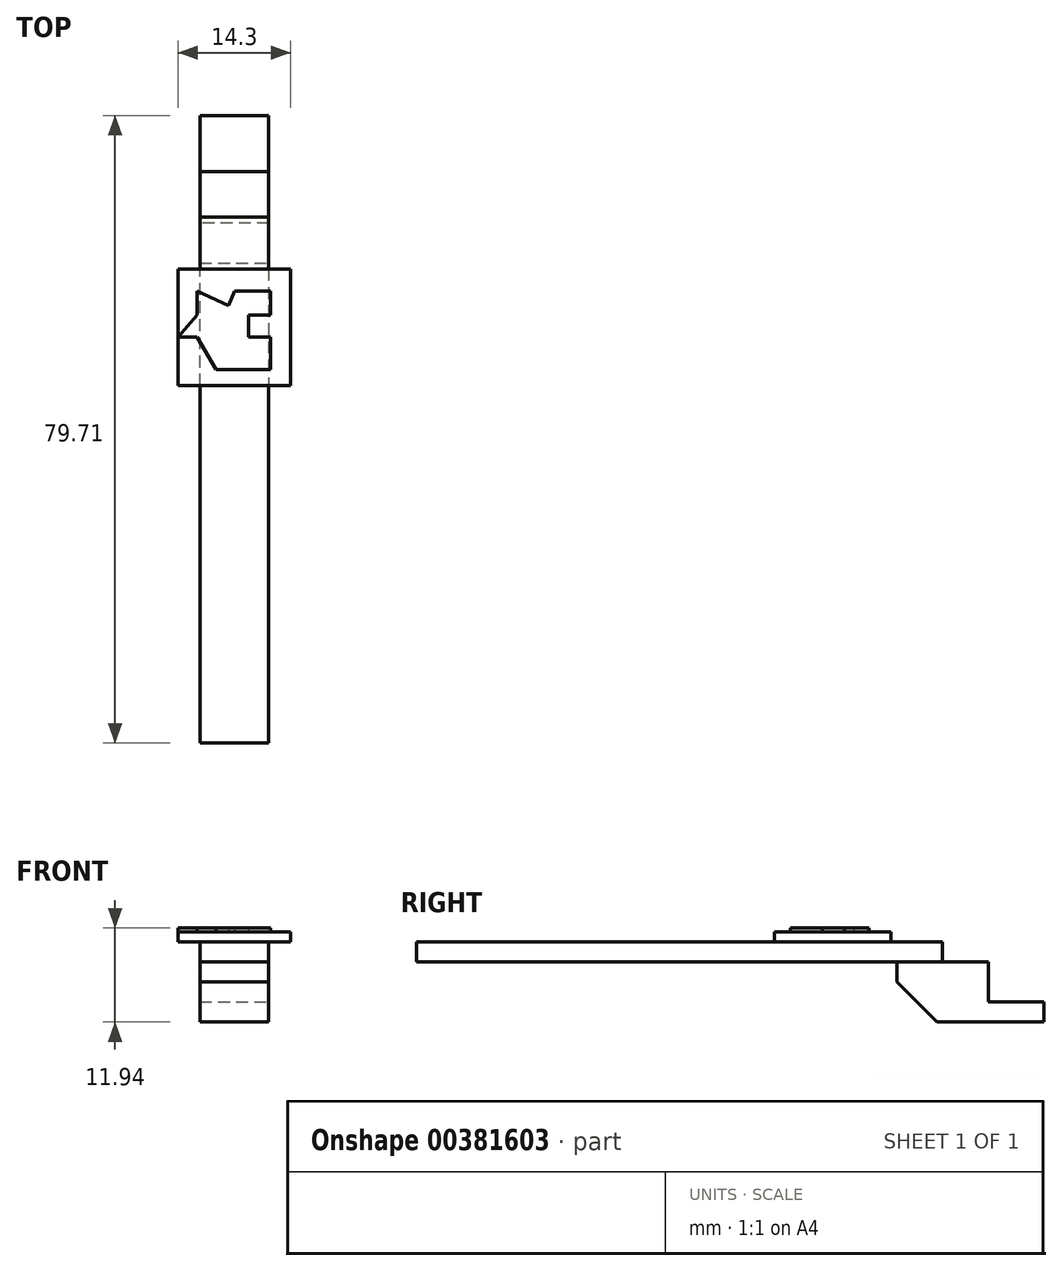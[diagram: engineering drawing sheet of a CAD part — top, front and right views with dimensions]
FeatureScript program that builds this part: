
annotation { "Feature Type Name" : "Feature", "Feature Type Description" : "" }
export const myFeature = defineFeature(function(context is Context, id is Id, definition is map)
    precondition{}
    {
        {
            var Q0;
            Q0=qCreatedBy(makeId("Top.planeOp"),FACE);
            var sketch = newSketch(context, id + "F0", { "sketchPlane" : qUnion([Q0])});
            skFitSpline(sketch, "E0", {"points": [v(0, 63.58) * mm, v(-18.17, 58.96) * mm, v(-23.3, 36.4) * mm, v(-12.53, 11.54) * mm, v(0, 6.16) * mm], "startDerivative": vector(-86.78, -3.86) * mm, "endDerivative": vector(63.99, -13.75) * mm});
            skFitSpline(sketch, "E1.MirrorCS", {"points": [v(0, 63.58) * mm, v(18.17, 58.96) * mm, v(23.3, 36.4) * mm, v(12.53, 11.54) * mm, v(0, 6.16) * mm], "startDerivative": vector(86.78, -3.86) * mm, "endDerivative": vector(-63.99, -13.75) * mm});
            skLineSegment(sketch, "E2", {"start": v(-4.37, 7.1) * mm, "end": v(-4.37, 0) * mm});
            skLineSegment(sketch, "E3", {"start": v(4.37, 7.1) * mm, "end": v(4.37, 0) * mm});
            skLineSegment(sketch, "E4", {"start": v(4.37, 0) * mm, "end": v(-4.37, 0) * mm});
            skLineSegment(sketch, "E5", {"start": v(-4.37, 7.1) * mm, "end": v(-4, 7.1) * mm});
            skLineSegment(sketch, "E6.trimOffspring", {"start": v(4, 7.1) * mm, "end": v(4.37, 7.1) * mm});
            skLineSegment(sketch, "E7", {"start": v(-4, 7.1) * mm, "end": v(4.37, 7.1) * mm});
            skLineSegment(sketch, "E8", {"start": v(-14.04, 53.47) * mm, "end": v(13.02, 53.47) * mm});
            skLineSegment(sketch, "E9", {"start": v(13.02, 21.06) * mm, "end": v(-14.04, 21.06) * mm});
            skLineSegment(sketch, "E10", {"start": v(-14.04, 49.9) * mm, "end": v(13.02, 49.9) * mm});
            skLineSegment(sketch, "E11", {"start": v(-14.04, 24.37) * mm, "end": v(13.02, 24.37) * mm});
            skLineSegment(sketch, "E12", {"start": v(-14.04, 34.58) * mm, "end": v(13.02, 34.58) * mm});
            skLineSegment(sketch, "E13", {"start": v(-14.04, 38.15) * mm, "end": v(13.02, 38.15) * mm});
            skLineSegment(sketch, "E14", {"start": v(13.02, 38.15) * mm, "end": v(13.02, 34.58) * mm});
            skLineSegment(sketch, "E15", {"start": v(13.02, 53.47) * mm, "end": v(13.02, 49.9) * mm});
            skLineSegment(sketch, "E16", {"start": v(-14.04, 53.47) * mm, "end": v(-14.04, 49.9) * mm});
            skLineSegment(sketch, "E17", {"start": v(-14.04, 38.15) * mm, "end": v(-14.04, 34.58) * mm});
            skLineSegment(sketch, "E18", {"start": v(-14.04, 24.37) * mm, "end": v(-14.04, 21.06) * mm});
            skLineSegment(sketch, "E19", {"start": v(13.02, 24.37) * mm, "end": v(13.02, 21.06) * mm});
            skLineSegment(sketch, "E20", {"start": v(-4.37, 0) * mm, "end": v(4.37, 0) * mm});
            skLineSegment(sketch, "E21", {"start": v(4.37, -11.61) * mm, "end": v(-4.37, -11.61) * mm});
            skLineSegment(sketch, "E22", {"start": v(-4.37, 0) * mm, "end": v(-4.37, -11.61) * mm});
            skLineSegment(sketch, "E23", {"start": v(4.37, -11.61) * mm, "end": v(4.37, 0) * mm});
            skSolve(sketch);
        }
        {
            var Q0;
            {var subQ0=sQuery(id+"F0.wireOp",EDGE,"E0");Q0=makeQuery(id+"F0.imprint","IMPRINT",FACE,{"disambiguationData":[TD([[makeQuery(id+"F0.imprint","IMPRINT",EDGE,{"derivedFrom":subQ0}),1.0]])]});}
            var Q1;
            Q1=makeQuery(id+"F0.imprint","IMPRINT",FACE,{"disambiguationData":[TD([[makeQuery(id+"F0.imprint","IMPRINT",EDGE,{"derivedFrom":sQuery(id+"F0.wireOp",EDGE,"E2")}),1.0]])]});
            extrude(context, id + "F1", {"entities" : qUnion([Q0, Q1]), "depth" : 2.54 * mm});
        }
        {
            var Q0;
            Q0=makeQuery(id+"F0.imprint","IMPRINT",FACE,{"disambiguationData":[TD([[makeQuery(id+"F0.imprint","IMPRINT",EDGE,{"derivedFrom":sQuery(id+"F0.wireOp",EDGE,"E21")}),-1.0]])]});
            extrude(context, id + "F2", {"entities" : qUnion([Q0]), "operationType" : NewBodyOperationType.ADD, "depth" : 7.62 * mm});
        }
        {
            var Q0;
            Q0=makeQuery(id+"F2.opExtrude","CAP_FACE",FACE,{"disambiguationData":[OSD([sQuery(id+"F0.wireOp",EDGE,"E21"),sQuery(id+"F0.wireOp",EDGE,"E22"),sQuery(id+"F0.wireOp",EDGE,"E20"),sQuery(id+"F0.wireOp",EDGE,"E23")])],"isStart":false});
            var sketch = newSketch(context, id + "F3", { "sketchPlane" : qUnion([Q0])});
            skLineSegment(sketch, "E24", {"start": v(-4.37, -5.8) * mm, "end": v(4.37, -5.8) * mm});
            skLineSegment(sketch, "E25", {"start": v(4.37, -5.8) * mm, "end": v(4.37, -72.6) * mm});
            skLineSegment(sketch, "E26", {"start": v(-4.37, -72.6) * mm, "end": v(-4.37, -5.8) * mm});
            skLineSegment(sketch, "E27", {"start": v(4.37, -70.31) * mm, "end": v(4.37, -72.6) * mm});
            skLineSegment(sketch, "E28", {"start": v(-4.37, -72.6) * mm, "end": v(4.37, -72.6) * mm});
            skSolve(sketch);
        }
        {
            var Q0;
            Q0 = qSketchRegion(id + "F3", true);
            extrude(context, id + "F4", {"entities" : qUnion([Q0]), "depth" : 2.54 * mm});
        }
        {
            var Q0;
            Q0=makeQuery(id+"F2.opExtrude","CAP_EDGE",EDGE,{"disambiguationData":[OSD([sQuery(id+"F0.wireOp",EDGE,"E21")])],"isStart":true});
            var Q1;
            Q1=makeQuery(id+"F2.opExtrude","CAP_EDGE",EDGE,{"disambiguationData":[OSD([sQuery(id+"F0.wireOp",EDGE,"E20")])],"isStart":false});
            chamfer(context, id + "F5", {"entities" : qUnion([Q0, Q1]), "width" : 5.08 * mm, "tangentPropagation" : true});
        }
        {
            var Q0;
            Q0=makeQuery(id+"F4.opExtrude","CAP_FACE",FACE,{"disambiguationData":[OSD([sQuery(id+"F3.wireOp",EDGE,"E24"),sQuery(id+"F3.wireOp",EDGE,"E25"),sQuery(id+"F3.wireOp",EDGE,"E26"),sQuery(id+"F3.wireOp",EDGE,"E27"),sQuery(id+"F3.wireOp",EDGE,"E28")])],"isStart":false});
            var sketch = newSketch(context, id + "F6", { "sketchPlane" : qUnion([Q0])});
            skLineSegment(sketch, "E29.bottom", {"start": v(7.15, -27.18) * mm, "end": v(-7.15, -27.18) * mm});
            skLineSegment(sketch, "E29.top", {"start": v(7.15, -12.38) * mm, "end": v(-7.15, -12.38) * mm});
            skLineSegment(sketch, "E29.left", {"start": v(7.15, -27.18) * mm, "end": v(7.15, -12.38) * mm});
            skLineSegment(sketch, "E29.right", {"start": v(-7.15, -27.18) * mm, "end": v(-7.15, -12.38) * mm});
            skPoint(sketch, "E29.middle", {"position": v(0, -19.78) * mm});
            skSolve(sketch);
        }
        {
            var Q0;
            Q0 = qSketchRegion(id + "F6", true);
            extrude(context, id + "F7", {"entities" : qUnion([Q0]), "operationType" : NewBodyOperationType.ADD, "depth" : 1.27 * mm});
        }
        {
            var Q0;
            Q0=makeQuery(id+"F7.opExtrude","CAP_FACE",FACE,{"disambiguationData":[OSD([sQuery(id+"F6.wireOp",EDGE,"E29.bottom"),sQuery(id+"F6.wireOp",EDGE,"E29.top"),sQuery(id+"F6.wireOp",EDGE,"E29.left"),sQuery(id+"F6.wireOp",EDGE,"E29.right")])],"isStart":false});
            var sketch = newSketch(context, id + "F8", { "sketchPlane" : qUnion([Q0])});
            skLineSegment(sketch, "E30", {"start": v(0, -15.19) * mm, "end": v(4.6, -15.19) * mm});
            skLineSegment(sketch, "E31", {"start": v(4.6, -15.19) * mm, "end": v(4.6, -18.25) * mm});
            skLineSegment(sketch, "E32", {"start": v(4.6, -18.25) * mm, "end": v(1.79, -18.25) * mm});
            skLineSegment(sketch, "E33", {"start": v(1.79, -18.25) * mm, "end": v(1.79, -21.06) * mm});
            skLineSegment(sketch, "E34", {"start": v(1.79, -21.06) * mm, "end": v(4.6, -21.06) * mm});
            skLineSegment(sketch, "E35", {"start": v(4.6, -21.06) * mm, "end": v(4.6, -25.14) * mm});
            skLineSegment(sketch, "E36", {"start": v(4.6, -25.14) * mm, "end": v(-2.3, -25.14) * mm});
            skLineSegment(sketch, "E37", {"start": v(-2.3, -25.14) * mm, "end": v(-2.3, -21.06) * mm});
            skLineSegment(sketch, "E38", {"start": v(-2.3, -21.06) * mm, "end": v(-7.15, -21.06) * mm});
            skLineSegment(sketch, "E39", {"start": v(-7.15, -21.06) * mm, "end": v(-4.72, -18.25) * mm});
            skPoint(sketch, "E39.endSnap0", {"position": v(-4.72, -21.06) * mm});
            skLineSegment(sketch, "E40", {"start": v(-4.72, -18.25) * mm, "end": v(-4.72, -15.19) * mm});
            skLineSegment(sketch, "E41", {"start": v(-4.72, -15.19) * mm, "end": v(1.79, -18.25) * mm});
            skLineSegment(sketch, "E42", {"start": v(0, -15.19) * mm, "end": v(-2.3, -21.06) * mm});
            skLineSegment(sketch, "E43", {"start": v(-2.3, -25.14) * mm, "end": v(-4.72, -21.06) * mm});
            skLineSegment(sketch, "E44", {"start": v(4.6, -25.14) * mm, "end": v(-2.3, -21.06) * mm});
            skSolve(sketch);
        }
        {
            var Q0;
            Q0 = qSketchRegion(id + "F8", true);
            extrude(context, id + "F9", {"entities" : qUnion([Q0]), "operationType" : NewBodyOperationType.ADD, "depth" : 0.5 * mm});
        }
    });
